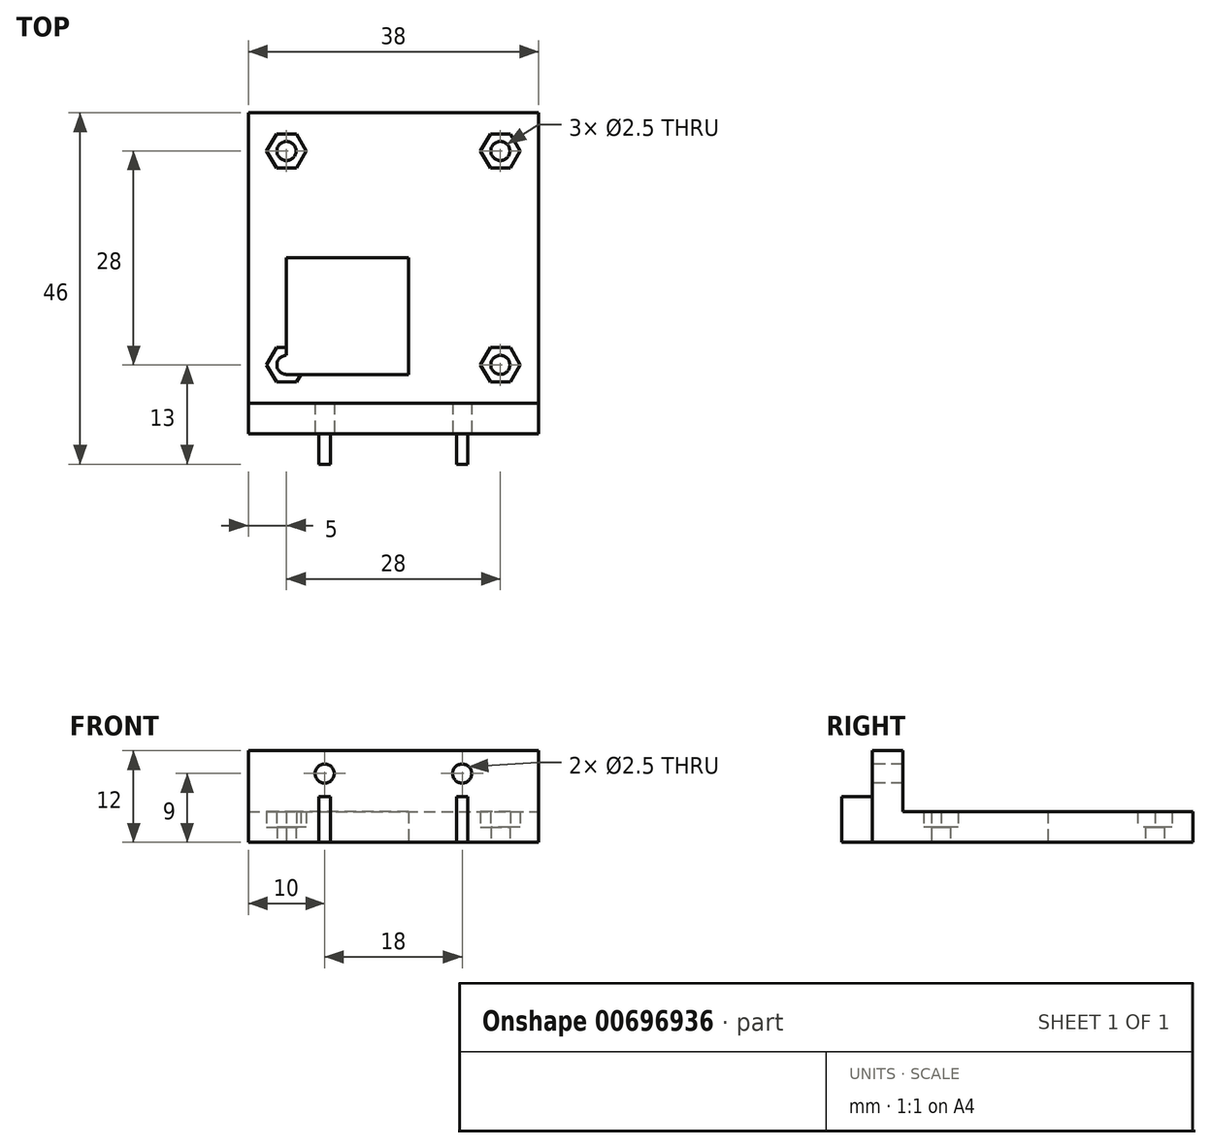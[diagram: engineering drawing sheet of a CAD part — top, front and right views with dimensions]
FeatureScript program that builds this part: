
annotation { "Feature Type Name" : "Feature", "Feature Type Description" : "" }
export const myFeature = defineFeature(function(context is Context, id is Id, definition is map)
    precondition{}
    {
        {
            var Q0;
            Q0=qCreatedBy(makeId("Top.planeOp"),FACE);
            var sketch = newSketch(context, id + "F0", { "sketchPlane" : qUnion([Q0])});
            skLineSegment(sketch, "E0.bottom", {"start": v(-19, 19) * mm, "end": v(19, 19) * mm});
            skLineSegment(sketch, "E0.top", {"start": v(-19, -23) * mm, "end": v(10, -23) * mm});
            skLineSegment(sketch, "E0.left", {"start": v(-19, 19) * mm, "end": v(-19, -23) * mm});
            skLineSegment(sketch, "E0.right", {"start": v(19, 19) * mm, "end": v(19, -23) * mm});
            skCircle(sketch, "E1", {"center": v(-14, 14) * mm, "radius": 1.25 * mm});
            skCircle(sketch, "E2", {"center": v(14, -14) * mm, "radius": 1.25 * mm});
            skCircle(sketch, "E3", {"center": v(-14, -14) * mm, "radius": 1.25 * mm});
            skLineSegment(sketch, "E4.bottom", {"start": v(10, -23) * mm, "end": v(12, -23) * mm});
            skLineSegment(sketch, "E5.trimOffspring", {"start": v(12, -23) * mm, "end": v(19, -23) * mm});
            skLineSegment(sketch, "E6", {"start": v(-14, -15.25) * mm, "end": v(2, -15.25) * mm});
            skLineSegment(sketch, "E7", {"start": v(2, -15.25) * mm, "end": v(2, 0) * mm});
            skLineSegment(sketch, "E8", {"start": v(2, 0) * mm, "end": v(-14, 0) * mm});
            skLineSegment(sketch, "E9", {"start": v(-14, 0) * mm, "end": v(-14, -12.75) * mm});
            skCircle(sketch, "E10", {"center": v(14, 14) * mm, "radius": 1.25 * mm});
            skSolve(sketch);
        }
        {
            var Q0;
            Q0=makeQuery(id+"F0.imprint","IMPRINT",FACE,{"disambiguationData":[TD([[makeQuery(id+"F0.imprint","IMPRINT",EDGE,{"derivedFrom":sQuery(id+"F0.wireOp",EDGE,"E0.bottom")}),-1.0]])]});
            extrude(context, id + "F1", {"entities" : qUnion([Q0]), "depth" : 2 * mm, "offsetDistance" : 25 * mm});
        }
        {
            var Q0;
            Q0=makeQuery(id+"F1.opExtrude","CAP_FACE",FACE,{"disambiguationData":[OSD([sQuery(id+"F0.wireOp",EDGE,"E0.bottom"),sQuery(id+"F0.wireOp",EDGE,"E0.top"),sQuery(id+"F0.wireOp",EDGE,"E0.left"),sQuery(id+"F0.wireOp",EDGE,"E0.right"),sQuery(id+"F0.wireOp",EDGE,"E1"),sQuery(id+"F0.wireOp",EDGE,"mzPumAdB-2kvE-liCs-SxzF-rTb1MTM4SGKX"),sQuery(id+"F0.wireOp",EDGE,"E2"),sQuery(id+"F0.wireOp",EDGE,"E3"),sQuery(id+"F0.wireOp",EDGE,"8egT6jjO-lD6n-W4nf-RZiV-oZyTSD4i0WGo"),sQuery(id+"F0.wireOp",EDGE,"10sKtK7S-OYZE-t4DD-BFJ0-RG0UWz4bh2i2"),sQuery(id+"F0.wireOp",EDGE,"PJqGtUYi-v4MC-r25S-MFk3-ZherLmqxgdLs"),sQuery(id+"F0.wireOp",EDGE,"uhhkMAZi-f0Kt-MIni-DVlv-2DqxlOX9QTJW")])],"isStart":false});
            var sketch = newSketch(context, id + "F2", { "sketchPlane" : qUnion([Q0])});
            skCircle(sketch, "E11.cCircle", {"center": v(-14, 14) * mm, "radius": 2.25 * mm, "construction": true});
            skLineSegment(sketch, "E11.0", {"start": v(-11.4, 14) * mm, "end": v(-12.7, 11.75) * mm});
            skLineSegment(sketch, "E11.1", {"start": v(-12.7, 11.75) * mm, "end": v(-15.3, 11.75) * mm});
            skLineSegment(sketch, "E11.2", {"start": v(-15.3, 11.75) * mm, "end": v(-16.6, 14) * mm});
            skLineSegment(sketch, "E11.3", {"start": v(-16.6, 14) * mm, "end": v(-15.3, 16.25) * mm});
            skLineSegment(sketch, "E11.4", {"start": v(-15.3, 16.25) * mm, "end": v(-12.7, 16.25) * mm});
            skLineSegment(sketch, "E11.5", {"start": v(-12.7, 16.25) * mm, "end": v(-11.4, 14) * mm});
            skPoint(sketch, "E11.0.midPoint", {"position": v(-12.05, 12.88) * mm});
            skCircle(sketch, "E12.cCircle", {"center": v(14, -14) * mm, "radius": 2.25 * mm, "construction": true});
            skLineSegment(sketch, "E12.0", {"start": v(16.6, -14) * mm, "end": v(15.3, -16.25) * mm});
            skLineSegment(sketch, "E12.1", {"start": v(15.3, -16.25) * mm, "end": v(12.7, -16.25) * mm});
            skLineSegment(sketch, "E12.2", {"start": v(12.7, -16.25) * mm, "end": v(11.4, -14) * mm});
            skLineSegment(sketch, "E12.3", {"start": v(11.4, -14) * mm, "end": v(12.7, -11.75) * mm});
            skLineSegment(sketch, "E12.4", {"start": v(12.7, -11.75) * mm, "end": v(15.3, -11.75) * mm});
            skLineSegment(sketch, "E12.5", {"start": v(15.3, -11.75) * mm, "end": v(16.6, -14) * mm});
            skPoint(sketch, "E12.0.midPoint", {"position": v(15.95, -15.13) * mm});
            skArc(sketch, "E13.cCircle", {"start": v(-14, -11.75) * mm, "mid": v(-15.95, -15.12) * mm, "end": v(-12.05, -15.13) * mm, "construction": true});
            skLineSegment(sketch, "E13.0", {"start": v(-12.05, -15.13) * mm, "end": v(-12.7, -16.25) * mm});
            skLineSegment(sketch, "E13.1", {"start": v(-12.7, -16.25) * mm, "end": v(-15.3, -16.25) * mm});
            skLineSegment(sketch, "E13.2", {"start": v(-15.3, -16.25) * mm, "end": v(-16.6, -14) * mm});
            skLineSegment(sketch, "E13.3", {"start": v(-16.6, -14) * mm, "end": v(-15.3, -11.75) * mm});
            skLineSegment(sketch, "E13.4", {"start": v(-15.3, -11.75) * mm, "end": v(-14, -11.75) * mm});
            skPoint(sketch, "E13.0.midPoint", {"position": v(-12.05, -15.13) * mm});
            skCircle(sketch, "E14.cCircle", {"center": v(14, 14) * mm, "radius": 2.25 * mm, "construction": true});
            skLineSegment(sketch, "E14.0", {"start": v(16.6, 14) * mm, "end": v(15.3, 11.75) * mm});
            skLineSegment(sketch, "E14.1", {"start": v(15.3, 11.75) * mm, "end": v(12.7, 11.75) * mm});
            skLineSegment(sketch, "E14.2", {"start": v(12.7, 11.75) * mm, "end": v(11.4, 14) * mm});
            skLineSegment(sketch, "E14.3", {"start": v(11.4, 14) * mm, "end": v(12.7, 16.25) * mm});
            skLineSegment(sketch, "E14.4", {"start": v(12.7, 16.25) * mm, "end": v(15.3, 16.25) * mm});
            skLineSegment(sketch, "E14.5", {"start": v(15.3, 16.25) * mm, "end": v(16.6, 14) * mm});
            skPoint(sketch, "E14.0.midPoint", {"position": v(15.95, 12.87) * mm});
            skLineSegment(sketch, "E15", {"start": v(-14, -11.75) * mm, "end": v(-14, 0) * mm});
            skLineSegment(sketch, "E16", {"start": v(-14, 0) * mm, "end": v(2, 0) * mm});
            skLineSegment(sketch, "E17", {"start": v(2, 0) * mm, "end": v(2, -15.25) * mm});
            skLineSegment(sketch, "E18", {"start": v(2, -15.25) * mm, "end": v(-12.05, -15.13) * mm});
            skPoint(sketch, "E19.orphan", {"position": v(-11.4, -14) * mm});
            skPoint(sketch, "E20.orphan", {"position": v(-12.7, -11.75) * mm});
            skSolve(sketch);
        }
        {
            var Q0;
            Q0=makeQuery(id+"F2.imprint","IMPRINT",FACE,{"disambiguationData":[TD([[makeQuery(id+"F2.imprint","IMPRINT",EDGE,{"derivedFrom":sQuery(id+"F2.wireOp",EDGE,"E11.0")}),1.0]])]});
            extrude(context, id + "F3", {"entities" : qUnion([Q0]), "operationType" : NewBodyOperationType.ADD, "depth" : 2 * mm, "offsetDistance" : 25 * mm});
        }
        {
            var Q0;
            Q0=qCreatedBy(makeId("Top.planeOp"),FACE);
            var sketch = newSketch(context, id + "F4", { "sketchPlane" : qUnion([Q0])});
            skLineSegment(sketch, "E21.bottom", {"start": v(-9.75, -27) * mm, "end": v(-8.25, -27) * mm});
            skLineSegment(sketch, "E21.top", {"start": v(-9.75, -23) * mm, "end": v(-8.25, -23) * mm});
            skLineSegment(sketch, "E21.left", {"start": v(-9.75, -27) * mm, "end": v(-9.75, -23) * mm});
            skLineSegment(sketch, "E21.right", {"start": v(-8.25, -27) * mm, "end": v(-8.25, -23) * mm});
            skLineSegment(sketch, "E22.bottom", {"start": v(8.25, -27) * mm, "end": v(9.75, -27) * mm});
            skLineSegment(sketch, "E22.top", {"start": v(8.25, -23) * mm, "end": v(9.75, -23) * mm});
            skLineSegment(sketch, "E22.left", {"start": v(8.25, -27) * mm, "end": v(8.25, -23) * mm});
            skLineSegment(sketch, "E22.right", {"start": v(9.75, -27) * mm, "end": v(9.75, -23) * mm});
            skSolve(sketch);
        }
        {
            var Q0;
            Q0 = qSketchRegion(id + "F4", true);
            var Q1;
            Q1=makeQuery(id+"F4.imprint","IMPRINT",FACE,{"disambiguationData":[TD([[makeQuery(id+"F4.imprint","IMPRINT",EDGE,{"derivedFrom":sQuery(id+"F4.wireOp",EDGE,"E21.bottom")}),1.0]])]});
            var Q2;
            Q2=makeQuery(id+"F4.imprint","IMPRINT",FACE,{"disambiguationData":[TD([[makeQuery(id+"F4.imprint","IMPRINT",EDGE,{"derivedFrom":sQuery(id+"F4.wireOp",EDGE,"E22.bottom")}),1.0]])]});
            extrude(context, id + "F5", {"entities" : qUnion([Q0, Q1, Q2]), "operationType" : NewBodyOperationType.ADD, "depth" : 6 * mm, "offsetDistance" : 25 * mm});
        }
        {
            var Q0;
            Q0=makeQuery(id+"F3.opExtrude","CAP_FACE",FACE,{"disambiguationData":[OSD([sQuery(id+"F0.wireOp",EDGE,"E0.bottom"),sQuery(id+"F0.wireOp",EDGE,"E0.top"),sQuery(id+"F0.wireOp",EDGE,"E0.left"),sQuery(id+"F0.wireOp",EDGE,"E0.right"),sQuery(id+"F0.wireOp",EDGE,"E4.bottom"),sQuery(id+"F0.wireOp",EDGE,"E5.trimOffspring"),sQuery(id+"F2.wireOp",EDGE,"E11.0"),sQuery(id+"F2.wireOp",EDGE,"E11.1"),sQuery(id+"F2.wireOp",EDGE,"E11.2"),sQuery(id+"F2.wireOp",EDGE,"E11.3"),sQuery(id+"F2.wireOp",EDGE,"E11.4"),sQuery(id+"F2.wireOp",EDGE,"E11.5"),sQuery(id+"F2.wireOp",EDGE,"e7400e80-2dd3-4249-9aee-6687b8e2abde.0"),sQuery(id+"F2.wireOp",EDGE,"e7400e80-2dd3-4249-9aee-6687b8e2abde.4"),sQuery(id+"F2.wireOp",EDGE,"E12.0"),sQuery(id+"F2.wireOp",EDGE,"E12.1"),sQuery(id+"F2.wireOp",EDGE,"E12.2"),sQuery(id+"F2.wireOp",EDGE,"E12.3"),sQuery(id+"F2.wireOp",EDGE,"E12.4"),sQuery(id+"F2.wireOp",EDGE,"E12.5"),sQuery(id+"F2.wireOp",EDGE,"E13.0"),sQuery(id+"F2.wireOp",EDGE,"E13.1"),sQuery(id+"F2.wireOp",EDGE,"E13.2"),sQuery(id+"F2.wireOp",EDGE,"E13.3"),sQuery(id+"F2.wireOp",EDGE,"E13.4"),sQuery(id+"F2.wireOp",EDGE,"E13.5"),sQuery(id+"F2.wireOp",EDGE,"u45mwJpR-4hri-nPhw-a0Wu-6H3Yn5iIWw1x"),sQuery(id+"F2.wireOp",EDGE,"7BPrz5BD-67Pe-mC3l-yr70-lKJzq79RhZ9O"),sQuery(id+"F2.wireOp",EDGE,"UTJzlvmh-0q5d-8xNu-N5Ug-ngr2AgKeCioK"),sQuery(id+"F2.wireOp",EDGE,"6YAPUVYF-E3ac-bmLB-Z8oO-yljCL34SMawK"),sQuery(id+"F2.wireOp",EDGE,"ipIDMWYB-x8j3-02ei-ePJO-RuIMmonXJsd8"),sQuery(id+"F2.wireOp",EDGE,"gymtX0lE-xo9j-RnEt-REuM-b4z01GF1RC5S"),sQuery(id+"F2.wireOp",EDGE,"jjdIzq7o-kBjN-mVln-LYgr-4L6YzwUkjhYh")])],"isStart":false});
            var sketch = newSketch(context, id + "F6", { "sketchPlane" : qUnion([Q0])});
            skLineSegment(sketch, "E23.bottom", {"start": v(-19, -23) * mm, "end": v(19, -23) * mm});
            skLineSegment(sketch, "E23.top", {"start": v(-19, -19) * mm, "end": v(19, -19) * mm});
            skLineSegment(sketch, "E23.left", {"start": v(-19, -23) * mm, "end": v(-19, -19) * mm});
            skLineSegment(sketch, "E23.right", {"start": v(19, -23) * mm, "end": v(19, -19) * mm});
            skSolve(sketch);
        }
        {
            var Q0;
            Q0 = qSketchRegion(id + "F6", true);
            extrude(context, id + "F7", {"entities" : qUnion([Q0]), "operationType" : NewBodyOperationType.ADD, "depth" : 8 * mm, "offsetDistance" : 25 * mm});
        }
        {
            var Q0;
            {var subQ0=sQuery(id+"F4.wireOp",EDGE,"E21.right");var subQ5=sQuery(id+"F0.wireOp",EDGE,"E5.trimOffspring");var subQ6=sQuery(id+"F0.wireOp",EDGE,"E4.bottom");var subQ7=sQuery(id+"F0.wireOp",EDGE,"E0.right");var subQ8=sQuery(id+"F0.wireOp",EDGE,"E0.left");var subQ9=sQuery(id+"F0.wireOp",EDGE,"E0.top");var subQ18=makeQuery(id+"F3.boolean.opBoolean","MERGE",FACE,{"derivedFrom":[makeQuery(id+"F1.opExtrude","SWEPT_FACE",FACE,{"disambiguationData":[OSD([subQ9,subQ6,subQ5])]}),makeQuery(id+"F3.opExtrude","SWEPT_FACE",FACE,{"disambiguationData":[OSD([subQ9,subQ6,subQ5])]})]});Q0=makeQuery(id+"F7.boolean.opBoolean","MERGE",FACE,{"derivedFrom":[makeQuery(id+"F5.boolean.opBoolean","SPLIT",FACE,{"disambiguationData":[TD([makeQuery(id+"F1.opExtrude","SWEPT_FACE",FACE,{"disambiguationData":[OSD([subQ8])]})])],"derivedFrom":subQ18}),makeQuery(id+"F5.boolean.opBoolean","SPLIT",FACE,{"disambiguationData":[TD([makeQuery(id+"F1.opExtrude","SWEPT_FACE",FACE,{"disambiguationData":[OSD([subQ7])]})])],"derivedFrom":subQ18}),makeQuery(id+"F5.boolean.opBoolean","SPLIT",FACE,{"disambiguationData":[TD([makeQuery(id+"F5.opExtrude","SWEPT_FACE",FACE,{"disambiguationData":[OSD([subQ0])]})])],"derivedFrom":subQ18}),makeQuery(id+"F7.opExtrude","SWEPT_FACE",FACE,{"disambiguationData":[OSD([sQuery(id+"F6.wireOp",EDGE,"E23.bottom")])]})]});}
            var sketch = newSketch(context, id + "F8", { "sketchPlane" : qUnion([Q0])});
            skCircle(sketch, "E24", {"center": v(-9, 9) * mm, "radius": 1.25 * mm});
            skCircle(sketch, "E25", {"center": v(9, 9) * mm, "radius": 1.25 * mm});
            skSolve(sketch);
        }
        {
            var Q0;
            Q0 = qSketchRegion(id + "F8", true);
            extrude(context, id + "F9", {"entities" : qUnion([Q0]), "operationType" : NewBodyOperationType.REMOVE, "oppositeDirection" : true, "depth" : 25 * mm, "offsetDistance" : 25 * mm});
        }
    });
